# Revit family: NBS_Senator_OffcTbls_Array_HalfRound750mm
name_source: partatom
category: Furniture
revit_build: Autodesk Revit 2018 (Build: 20190510_1515(x64)
units: mm (PartAtom-declared; Revit-internal decimal feet)

## family parameters
Always vertical = Yes
Cut with Voids When Loaded = No
Room Calculation Point = No
Shared = No
Work Plane-Based = No

## types (1)
- Array-HalfRound750mm_ARC1507HR
    Application = Office and educational settings
    AssetType = Fixed
    Attachment = 1000 mm  [stored 3.28084 ft]
    BIMObjectName = NBS_TheSenatorGroup_OfficeTables_Array-HalfRound750mm_ARC1507HR
    Category = Pr_40_50_21_60:Office tables
    CodePerformance = BS EN 15372, BS EN 6396
    Color = Silver, white, black
    Description = Half round table
    DurationUnit = year
    ExpectedLife = 15
    Features = Rigid cast aluminium frame, fully integrated cable management, lockable brake castors, nesting capabilities, gas assisted lift, single hand to unlock, flexible swipe-in cable risers, 25 mm MFC tops
    Finish = Highland oak, beech, maple, white, autumn, winter oak, strata oak, mocha, carini walnutm hacienda white, denim, clay, lemon sorbet, light grey
    FrameMaterial = NBS_SenatorGroup_Aluminium_Flat_Silver
    IfcExportAs = IfcFurnitureType
    IfcExportType = TABLE
    InternalWheelMaterial = NBS_SenatorGroup_Aluminium_Flat_Silver
    IsBuiltIn = No
    ManufacturerName = The Senator Group
    ManufacturerURL = www.senator.co.uk
    Material = Aluminium, wood
    ModelNumber = ARC1507HR
    ModelReference = Array-HalfRound750mm_ARC1507HR
    NBSCertification = www.nationalbimlibrary.com/cert/f3rtd0y5
    NBSDescription = Office tables
    NBSReference = 45-35-20/340
    Name = OfficeTables_Array-HalfRound750mm_ARC1507HR_TheSenatorGroup
    NominalDepth = 750 mm  [stored 2.46063 ft]
    NominalHeight = 740 mm
    NominalLength = 1500 mm  [stored 4.92126 ft]
    NominalWidth = 1500 mm  [stored 4.92126 ft]
    NumberOfChairs = 0
    OptionalExtras = Below desk power complete with flip unit, in-surface power unit, flip in-surface power unit
    ProductInformation = http://www.thesenatorgroup.com
    Size = 750 x 1500 mm
    SpecifiableFeatures = Quadrants, modesty panels, aluminium cable riser
    Status = UNSET
    Style = Table
    SustainabilityPerformance = 99% recyclable
    TableDepth = 750 mm  [stored 2.46063 ft]
    TableTopMaterial = NBS_SenatorGroup_Wood_Dark_Mocha
    TableTopThickness = 25 mm
    TableWidth = 1500 mm  [stored 4.92126 ft]
    Uniclass2015Code = Pr_40_50_21_60
    Uniclass2015Title = Office tables
    Uniclass2015Version = Products v1.16
    Version = 1
    WarrantyDescription = Senator warrants that its manufactured products are free from manufacturing defects - in materials or workmanship - for a period of ten (10) years on Senator Seating ranges; and fifteen (15) years on Senator Desking ranges - exceptions are listed below. Senator will repair or replace (at Senator’s sole discretion) with comparable free of charge materials / components, any product / component, which fails under normal use in a single shift environment, as a result of a defect in the materials and / or workmanship
    WarrantyDurationParts = 15
    WarrantyDurationUnit = year
    WheelBrakeMaterial = NBS_SenatorGroup_Plastic_Grey
    WheelMaterial = NBS_SenatorGroup_Rubber_Black
    WorksurfaceArea = 0 m²

note: [stored X ft] marks values corroborated as IEEE doubles in the binary element streams (Revit-internal decimal feet)

## geometry (parser evidence)
native form markers: Sweep x11
no freeform markers — native parametric forms only
